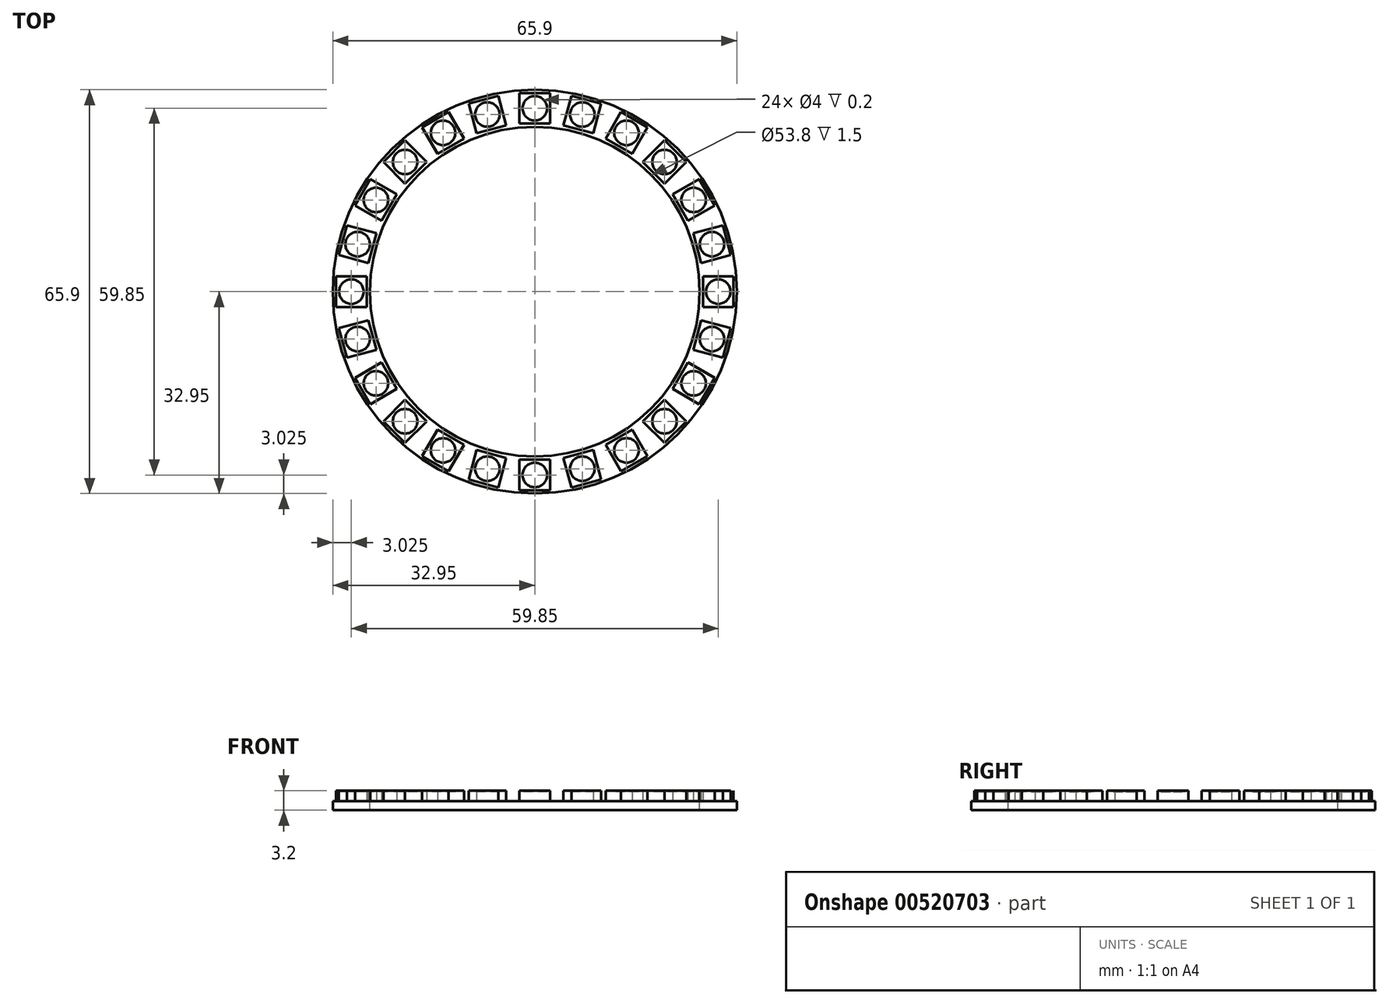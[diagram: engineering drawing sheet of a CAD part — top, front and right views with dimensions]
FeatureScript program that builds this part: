
annotation { "Feature Type Name" : "Feature", "Feature Type Description" : "" }
export const myFeature = defineFeature(function(context is Context, id is Id, definition is map)
    precondition{}
    {
        {
            assignVariable(context, id + "F0", {"name" : "LED_PCB_height", "anyValue" : 1.5 * mm});
        }
        {
            assignVariable(context, id + "F1", {"name" : "LED_case_height", "anyValue" : 1.7 * mm});
        }
        {
            assignVariable(context, id + "F2", {"name" : "LED_lens_height", "anyValue" : 1.5 * mm});
        }
        {
            var Q0;
            Q0=qCreatedBy(makeId("Top.planeOp"),FACE);
            var sketch = newSketch(context, id + "F3", { "sketchPlane" : qUnion([Q0])});
            skCircle(sketch, "E0", {"center": v(0, 0) * mm, "radius": 26.9 * mm});
            skCircle(sketch, "E1", {"center": v(0, 0) * mm, "radius": 32.95 * mm});
            skLineSegment(sketch, "E2.bottom", {"start": v(-2.5, 32.43) * mm, "end": v(2.5, 32.43) * mm});
            skLineSegment(sketch, "E2.top", {"start": v(-2.5, 27.43) * mm, "end": v(2.5, 27.43) * mm});
            skLineSegment(sketch, "E2.left", {"start": v(-2.5, 32.43) * mm, "end": v(-2.5, 27.43) * mm});
            skLineSegment(sketch, "E2.right", {"start": v(2.5, 32.43) * mm, "end": v(2.5, 27.43) * mm});
            skLineSegment(sketch, "E3", {"start": v(0, 32.43) * mm, "end": v(0, 32.95) * mm, "construction": true});
            skLineSegment(sketch, "E4", {"start": v(0, 27.43) * mm, "end": v(0, 26.9) * mm, "construction": true});
            skLineSegment(sketch, "E5", {"start": v(-2.5, 32.43) * mm, "end": v(2.5, 27.43) * mm, "construction": true});
            skLineSegment(sketch, "E6", {"start": v(2.5, 32.43) * mm, "end": v(-2.5, 27.43) * mm, "construction": true});
            skCircle(sketch, "E7", {"center": v(0, 29.93) * mm, "radius": 2 * mm});
            skCircle(sketch, "E8.1.0", {"center": v(-7.75, 28.9) * mm, "radius": 2 * mm});
            skLineSegment(sketch, "E8.1.1", {"start": v(-10.8, 30.67) * mm, "end": v(-5.98, 31.97) * mm});
            skLineSegment(sketch, "E8.1.2", {"start": v(-10.8, 30.67) * mm, "end": v(-9.51, 25.84) * mm});
            skLineSegment(sketch, "E8.1.3", {"start": v(-9.51, 25.84) * mm, "end": v(-4.68, 27.14) * mm});
            skLineSegment(sketch, "E8.1.4", {"start": v(-5.98, 31.97) * mm, "end": v(-4.68, 27.14) * mm});
            skCircle(sketch, "E8.2.0", {"center": v(-14.96, 25.92) * mm, "radius": 2 * mm});
            skLineSegment(sketch, "E8.2.1", {"start": v(-18.38, 26.83) * mm, "end": v(-14.05, 29.33) * mm});
            skLineSegment(sketch, "E8.2.2", {"start": v(-18.38, 26.83) * mm, "end": v(-15.88, 22.5) * mm});
            skLineSegment(sketch, "E8.2.3", {"start": v(-15.88, 22.5) * mm, "end": v(-11.55, 25) * mm});
            skLineSegment(sketch, "E8.2.4", {"start": v(-14.05, 29.33) * mm, "end": v(-11.55, 25) * mm});
            skCircle(sketch, "E8.3.0", {"center": v(-21.16, 21.16) * mm, "radius": 2 * mm});
            skLineSegment(sketch, "E8.3.1", {"start": v(-24.7, 21.16) * mm, "end": v(-21.16, 24.7) * mm});
            skLineSegment(sketch, "E8.3.2", {"start": v(-24.7, 21.16) * mm, "end": v(-21.16, 17.62) * mm});
            skLineSegment(sketch, "E8.3.3", {"start": v(-21.16, 17.62) * mm, "end": v(-17.62, 21.16) * mm});
            skLineSegment(sketch, "E8.3.4", {"start": v(-21.16, 24.7) * mm, "end": v(-17.62, 21.16) * mm});
            skCircle(sketch, "E8.4.0", {"center": v(-25.92, 14.96) * mm, "radius": 2 * mm});
            skLineSegment(sketch, "E8.4.1", {"start": v(-29.33, 14.05) * mm, "end": v(-26.83, 18.38) * mm});
            skLineSegment(sketch, "E8.4.2", {"start": v(-29.33, 14.05) * mm, "end": v(-25, 11.55) * mm});
            skLineSegment(sketch, "E8.4.3", {"start": v(-25, 11.55) * mm, "end": v(-22.5, 15.88) * mm});
            skLineSegment(sketch, "E8.4.4", {"start": v(-26.83, 18.38) * mm, "end": v(-22.5, 15.88) * mm});
            skCircle(sketch, "E8.5.0", {"center": v(-28.9, 7.75) * mm, "radius": 2 * mm});
            skLineSegment(sketch, "E8.5.1", {"start": v(-31.97, 5.98) * mm, "end": v(-30.67, 10.8) * mm});
            skLineSegment(sketch, "E8.5.2", {"start": v(-31.97, 5.98) * mm, "end": v(-27.14, 4.68) * mm});
            skLineSegment(sketch, "E8.5.3", {"start": v(-27.14, 4.68) * mm, "end": v(-25.84, 9.51) * mm});
            skLineSegment(sketch, "E8.5.4", {"start": v(-30.67, 10.8) * mm, "end": v(-25.84, 9.51) * mm});
            skCircle(sketch, "E8.6.0", {"center": v(-29.93, 0) * mm, "radius": 2 * mm});
            skLineSegment(sketch, "E8.6.1", {"start": v(-32.43, -2.5) * mm, "end": v(-32.43, 2.5) * mm});
            skLineSegment(sketch, "E8.6.2", {"start": v(-32.43, -2.5) * mm, "end": v(-27.43, -2.5) * mm});
            skLineSegment(sketch, "E8.6.3", {"start": v(-27.43, -2.5) * mm, "end": v(-27.43, 2.5) * mm});
            skLineSegment(sketch, "E8.6.4", {"start": v(-32.43, 2.5) * mm, "end": v(-27.43, 2.5) * mm});
            skCircle(sketch, "E8.7.0", {"center": v(-28.9, -7.75) * mm, "radius": 2 * mm});
            skLineSegment(sketch, "E8.7.1", {"start": v(-30.67, -10.8) * mm, "end": v(-31.97, -5.98) * mm});
            skLineSegment(sketch, "E8.7.2", {"start": v(-30.67, -10.8) * mm, "end": v(-25.84, -9.51) * mm});
            skLineSegment(sketch, "E8.7.3", {"start": v(-25.84, -9.51) * mm, "end": v(-27.14, -4.68) * mm});
            skLineSegment(sketch, "E8.7.4", {"start": v(-31.97, -5.98) * mm, "end": v(-27.14, -4.68) * mm});
            skCircle(sketch, "E8.8.0", {"center": v(-25.92, -14.96) * mm, "radius": 2 * mm});
            skLineSegment(sketch, "E8.8.1", {"start": v(-26.83, -18.38) * mm, "end": v(-29.33, -14.05) * mm});
            skLineSegment(sketch, "E8.8.2", {"start": v(-26.83, -18.38) * mm, "end": v(-22.5, -15.88) * mm});
            skLineSegment(sketch, "E8.8.3", {"start": v(-22.5, -15.88) * mm, "end": v(-25, -11.55) * mm});
            skLineSegment(sketch, "E8.8.4", {"start": v(-29.33, -14.05) * mm, "end": v(-25, -11.55) * mm});
            skCircle(sketch, "E8.9.0", {"center": v(-21.16, -21.16) * mm, "radius": 2 * mm});
            skLineSegment(sketch, "E8.9.1", {"start": v(-21.16, -24.7) * mm, "end": v(-24.7, -21.16) * mm});
            skLineSegment(sketch, "E8.9.2", {"start": v(-21.16, -24.7) * mm, "end": v(-17.62, -21.16) * mm});
            skLineSegment(sketch, "E8.9.3", {"start": v(-17.62, -21.16) * mm, "end": v(-21.16, -17.62) * mm});
            skLineSegment(sketch, "E8.9.4", {"start": v(-24.7, -21.16) * mm, "end": v(-21.16, -17.62) * mm});
            skCircle(sketch, "E8.10.0", {"center": v(-14.96, -25.92) * mm, "radius": 2 * mm});
            skLineSegment(sketch, "E8.10.1", {"start": v(-14.05, -29.33) * mm, "end": v(-18.38, -26.83) * mm});
            skLineSegment(sketch, "E8.10.2", {"start": v(-14.05, -29.33) * mm, "end": v(-11.55, -25) * mm});
            skLineSegment(sketch, "E8.10.3", {"start": v(-11.55, -25) * mm, "end": v(-15.88, -22.5) * mm});
            skLineSegment(sketch, "E8.10.4", {"start": v(-18.38, -26.83) * mm, "end": v(-15.88, -22.5) * mm});
            skCircle(sketch, "E8.11.0", {"center": v(-7.75, -28.9) * mm, "radius": 2 * mm});
            skLineSegment(sketch, "E8.11.1", {"start": v(-5.98, -31.97) * mm, "end": v(-10.8, -30.67) * mm});
            skLineSegment(sketch, "E8.11.2", {"start": v(-5.98, -31.97) * mm, "end": v(-4.68, -27.14) * mm});
            skLineSegment(sketch, "E8.11.3", {"start": v(-4.68, -27.14) * mm, "end": v(-9.51, -25.84) * mm});
            skLineSegment(sketch, "E8.11.4", {"start": v(-10.8, -30.67) * mm, "end": v(-9.51, -25.84) * mm});
            skCircle(sketch, "E8.12.0", {"center": v(0, -29.93) * mm, "radius": 2 * mm});
            skLineSegment(sketch, "E8.12.1", {"start": v(2.5, -32.43) * mm, "end": v(-2.5, -32.43) * mm});
            skLineSegment(sketch, "E8.12.2", {"start": v(2.5, -32.43) * mm, "end": v(2.5, -27.43) * mm});
            skLineSegment(sketch, "E8.12.3", {"start": v(2.5, -27.43) * mm, "end": v(-2.5, -27.43) * mm});
            skLineSegment(sketch, "E8.12.4", {"start": v(-2.5, -32.43) * mm, "end": v(-2.5, -27.43) * mm});
            skCircle(sketch, "E8.13.0", {"center": v(7.75, -28.9) * mm, "radius": 2 * mm});
            skLineSegment(sketch, "E8.13.1", {"start": v(10.8, -30.67) * mm, "end": v(5.98, -31.97) * mm});
            skLineSegment(sketch, "E8.13.2", {"start": v(10.8, -30.67) * mm, "end": v(9.51, -25.84) * mm});
            skLineSegment(sketch, "E8.13.3", {"start": v(9.51, -25.84) * mm, "end": v(4.68, -27.14) * mm});
            skLineSegment(sketch, "E8.13.4", {"start": v(5.98, -31.97) * mm, "end": v(4.68, -27.14) * mm});
            skCircle(sketch, "E8.14.0", {"center": v(14.96, -25.92) * mm, "radius": 2 * mm});
            skLineSegment(sketch, "E8.14.1", {"start": v(18.38, -26.83) * mm, "end": v(14.05, -29.33) * mm});
            skLineSegment(sketch, "E8.14.2", {"start": v(18.38, -26.83) * mm, "end": v(15.88, -22.5) * mm});
            skLineSegment(sketch, "E8.14.3", {"start": v(15.88, -22.5) * mm, "end": v(11.55, -25) * mm});
            skLineSegment(sketch, "E8.14.4", {"start": v(14.05, -29.33) * mm, "end": v(11.55, -25) * mm});
            skCircle(sketch, "E8.15.0", {"center": v(21.16, -21.16) * mm, "radius": 2 * mm});
            skLineSegment(sketch, "E8.15.1", {"start": v(24.7, -21.16) * mm, "end": v(21.16, -24.7) * mm});
            skLineSegment(sketch, "E8.15.2", {"start": v(24.7, -21.16) * mm, "end": v(21.16, -17.62) * mm});
            skLineSegment(sketch, "E8.15.3", {"start": v(21.16, -17.62) * mm, "end": v(17.62, -21.16) * mm});
            skLineSegment(sketch, "E8.15.4", {"start": v(21.16, -24.7) * mm, "end": v(17.62, -21.16) * mm});
            skCircle(sketch, "E8.16.0", {"center": v(25.92, -14.96) * mm, "radius": 2 * mm});
            skLineSegment(sketch, "E8.16.1", {"start": v(29.33, -14.05) * mm, "end": v(26.83, -18.38) * mm});
            skLineSegment(sketch, "E8.16.2", {"start": v(29.33, -14.05) * mm, "end": v(25, -11.55) * mm});
            skLineSegment(sketch, "E8.16.3", {"start": v(25, -11.55) * mm, "end": v(22.5, -15.88) * mm});
            skLineSegment(sketch, "E8.16.4", {"start": v(26.83, -18.38) * mm, "end": v(22.5, -15.88) * mm});
            skCircle(sketch, "E8.17.0", {"center": v(28.9, -7.75) * mm, "radius": 2 * mm});
            skLineSegment(sketch, "E8.17.1", {"start": v(31.97, -5.98) * mm, "end": v(30.67, -10.8) * mm});
            skLineSegment(sketch, "E8.17.2", {"start": v(31.97, -5.98) * mm, "end": v(27.14, -4.68) * mm});
            skLineSegment(sketch, "E8.17.3", {"start": v(27.14, -4.68) * mm, "end": v(25.84, -9.51) * mm});
            skLineSegment(sketch, "E8.17.4", {"start": v(30.67, -10.8) * mm, "end": v(25.84, -9.51) * mm});
            skCircle(sketch, "E8.18.0", {"center": v(29.93, 0) * mm, "radius": 2 * mm});
            skLineSegment(sketch, "E8.18.1", {"start": v(32.43, 2.5) * mm, "end": v(32.43, -2.5) * mm});
            skLineSegment(sketch, "E8.18.2", {"start": v(32.43, 2.5) * mm, "end": v(27.43, 2.5) * mm});
            skLineSegment(sketch, "E8.18.3", {"start": v(27.43, 2.5) * mm, "end": v(27.43, -2.5) * mm});
            skLineSegment(sketch, "E8.18.4", {"start": v(32.43, -2.5) * mm, "end": v(27.43, -2.5) * mm});
            skCircle(sketch, "E8.19.0", {"center": v(28.9, 7.75) * mm, "radius": 2 * mm});
            skLineSegment(sketch, "E8.19.1", {"start": v(30.67, 10.8) * mm, "end": v(31.97, 5.98) * mm});
            skLineSegment(sketch, "E8.19.2", {"start": v(30.67, 10.8) * mm, "end": v(25.84, 9.51) * mm});
            skLineSegment(sketch, "E8.19.3", {"start": v(25.84, 9.51) * mm, "end": v(27.14, 4.68) * mm});
            skLineSegment(sketch, "E8.19.4", {"start": v(31.97, 5.98) * mm, "end": v(27.14, 4.68) * mm});
            skCircle(sketch, "E8.20.0", {"center": v(25.92, 14.96) * mm, "radius": 2 * mm});
            skLineSegment(sketch, "E8.20.1", {"start": v(26.83, 18.38) * mm, "end": v(29.33, 14.05) * mm});
            skLineSegment(sketch, "E8.20.2", {"start": v(26.83, 18.38) * mm, "end": v(22.5, 15.88) * mm});
            skLineSegment(sketch, "E8.20.3", {"start": v(22.5, 15.88) * mm, "end": v(25, 11.55) * mm});
            skLineSegment(sketch, "E8.20.4", {"start": v(29.33, 14.05) * mm, "end": v(25, 11.55) * mm});
            skCircle(sketch, "E8.21.0", {"center": v(21.16, 21.16) * mm, "radius": 2 * mm});
            skLineSegment(sketch, "E8.21.1", {"start": v(21.16, 24.7) * mm, "end": v(24.7, 21.16) * mm});
            skLineSegment(sketch, "E8.21.2", {"start": v(21.16, 24.7) * mm, "end": v(17.62, 21.16) * mm});
            skLineSegment(sketch, "E8.21.3", {"start": v(17.62, 21.16) * mm, "end": v(21.16, 17.62) * mm});
            skLineSegment(sketch, "E8.21.4", {"start": v(24.7, 21.16) * mm, "end": v(21.16, 17.62) * mm});
            skCircle(sketch, "E8.22.0", {"center": v(14.96, 25.92) * mm, "radius": 2 * mm});
            skLineSegment(sketch, "E8.22.1", {"start": v(14.05, 29.33) * mm, "end": v(18.38, 26.83) * mm});
            skLineSegment(sketch, "E8.22.2", {"start": v(14.05, 29.33) * mm, "end": v(11.55, 25) * mm});
            skLineSegment(sketch, "E8.22.3", {"start": v(11.55, 25) * mm, "end": v(15.88, 22.5) * mm});
            skLineSegment(sketch, "E8.22.4", {"start": v(18.38, 26.83) * mm, "end": v(15.88, 22.5) * mm});
            skCircle(sketch, "E8.23.0", {"center": v(7.75, 28.9) * mm, "radius": 2 * mm});
            skLineSegment(sketch, "E8.23.1", {"start": v(5.98, 31.97) * mm, "end": v(10.8, 30.67) * mm});
            skLineSegment(sketch, "E8.23.2", {"start": v(5.98, 31.97) * mm, "end": v(4.68, 27.14) * mm});
            skLineSegment(sketch, "E8.23.3", {"start": v(4.68, 27.14) * mm, "end": v(9.51, 25.84) * mm});
            skLineSegment(sketch, "E8.23.4", {"start": v(10.8, 30.67) * mm, "end": v(9.51, 25.84) * mm});
            skSolve(sketch);
        }
        {
            var Q0;
            Q0=makeQuery(id+"F3.imprint","IMPRINT",FACE,{"disambiguationData":[TD([[makeQuery(id+"F3.imprint","IMPRINT",EDGE,{"derivedFrom":sQuery(id+"F3.wireOp",EDGE,"E0")}),-1.0]])]});
            var Q1;
            Q1=makeQuery(id+"F3.imprint","IMPRINT",FACE,{"disambiguationData":[TD([[makeQuery(id+"F3.imprint","IMPRINT",EDGE,{"derivedFrom":sQuery(id+"F3.wireOp",EDGE,"E8.3.0")}),1.0]])]});
            var Q2;
            Q2=makeQuery(id+"F3.imprint","IMPRINT",FACE,{"disambiguationData":[TD([[makeQuery(id+"F3.imprint","IMPRINT",EDGE,{"derivedFrom":sQuery(id+"F3.wireOp",EDGE,"E8.3.0")}),-1.0]])]});
            var Q3;
            Q3=makeQuery(id+"F3.imprint","IMPRINT",FACE,{"disambiguationData":[TD([[makeQuery(id+"F3.imprint","IMPRINT",EDGE,{"derivedFrom":sQuery(id+"F3.wireOp",EDGE,"E8.2.0")}),-1.0]])]});
            var Q4;
            Q4=makeQuery(id+"F3.imprint","IMPRINT",FACE,{"disambiguationData":[TD([[makeQuery(id+"F3.imprint","IMPRINT",EDGE,{"derivedFrom":sQuery(id+"F3.wireOp",EDGE,"E8.2.0")}),1.0]])]});
            var Q5;
            Q5=makeQuery(id+"F3.imprint","IMPRINT",FACE,{"disambiguationData":[TD([[makeQuery(id+"F3.imprint","IMPRINT",EDGE,{"derivedFrom":sQuery(id+"F3.wireOp",EDGE,"E8.1.0")}),-1.0]])]});
            var Q6;
            Q6=makeQuery(id+"F3.imprint","IMPRINT",FACE,{"disambiguationData":[TD([[makeQuery(id+"F3.imprint","IMPRINT",EDGE,{"derivedFrom":sQuery(id+"F3.wireOp",EDGE,"E8.1.0")}),1.0]])]});
            var Q7;
            Q7=makeQuery(id+"F3.imprint","IMPRINT",FACE,{"disambiguationData":[TD([[makeQuery(id+"F3.imprint","IMPRINT",EDGE,{"derivedFrom":sQuery(id+"F3.wireOp",EDGE,"E7")}),1.0]])]});
            var Q8;
            Q8=makeQuery(id+"F3.imprint","IMPRINT",FACE,{"disambiguationData":[TD([[makeQuery(id+"F3.imprint","IMPRINT",EDGE,{"derivedFrom":sQuery(id+"F3.wireOp",EDGE,"E2.bottom")}),-1.0]])]});
            var Q9;
            Q9=makeQuery(id+"F3.imprint","IMPRINT",FACE,{"disambiguationData":[TD([[makeQuery(id+"F3.imprint","IMPRINT",EDGE,{"derivedFrom":sQuery(id+"F3.wireOp",EDGE,"E8.23.0")}),1.0]])]});
            var Q10;
            Q10=makeQuery(id+"F3.imprint","IMPRINT",FACE,{"disambiguationData":[TD([[makeQuery(id+"F3.imprint","IMPRINT",EDGE,{"derivedFrom":sQuery(id+"F3.wireOp",EDGE,"E8.23.0")}),-1.0]])]});
            var Q11;
            Q11=makeQuery(id+"F3.imprint","IMPRINT",FACE,{"disambiguationData":[TD([[makeQuery(id+"F3.imprint","IMPRINT",EDGE,{"derivedFrom":sQuery(id+"F3.wireOp",EDGE,"E8.22.0")}),1.0]])]});
            var Q12;
            Q12=makeQuery(id+"F3.imprint","IMPRINT",FACE,{"disambiguationData":[TD([[makeQuery(id+"F3.imprint","IMPRINT",EDGE,{"derivedFrom":sQuery(id+"F3.wireOp",EDGE,"E8.22.0")}),-1.0]])]});
            var Q13;
            Q13=makeQuery(id+"F3.imprint","IMPRINT",FACE,{"disambiguationData":[TD([[makeQuery(id+"F3.imprint","IMPRINT",EDGE,{"derivedFrom":sQuery(id+"F3.wireOp",EDGE,"E8.21.0")}),1.0]])]});
            var Q14;
            Q14=makeQuery(id+"F3.imprint","IMPRINT",FACE,{"disambiguationData":[TD([[makeQuery(id+"F3.imprint","IMPRINT",EDGE,{"derivedFrom":sQuery(id+"F3.wireOp",EDGE,"E8.21.0")}),-1.0]])]});
            var Q15;
            Q15=makeQuery(id+"F3.imprint","IMPRINT",FACE,{"disambiguationData":[TD([[makeQuery(id+"F3.imprint","IMPRINT",EDGE,{"derivedFrom":sQuery(id+"F3.wireOp",EDGE,"E8.20.0")}),1.0]])]});
            var Q16;
            Q16=makeQuery(id+"F3.imprint","IMPRINT",FACE,{"disambiguationData":[TD([[makeQuery(id+"F3.imprint","IMPRINT",EDGE,{"derivedFrom":sQuery(id+"F3.wireOp",EDGE,"E8.20.0")}),-1.0]])]});
            var Q17;
            Q17=makeQuery(id+"F3.imprint","IMPRINT",FACE,{"disambiguationData":[TD([[makeQuery(id+"F3.imprint","IMPRINT",EDGE,{"derivedFrom":sQuery(id+"F3.wireOp",EDGE,"E8.19.0")}),1.0]])]});
            var Q18;
            Q18=makeQuery(id+"F3.imprint","IMPRINT",FACE,{"disambiguationData":[TD([[makeQuery(id+"F3.imprint","IMPRINT",EDGE,{"derivedFrom":sQuery(id+"F3.wireOp",EDGE,"E8.19.0")}),-1.0]])]});
            var Q19;
            Q19=makeQuery(id+"F3.imprint","IMPRINT",FACE,{"disambiguationData":[TD([[makeQuery(id+"F3.imprint","IMPRINT",EDGE,{"derivedFrom":sQuery(id+"F3.wireOp",EDGE,"E8.18.0")}),1.0]])]});
            var Q20;
            Q20=makeQuery(id+"F3.imprint","IMPRINT",FACE,{"disambiguationData":[TD([[makeQuery(id+"F3.imprint","IMPRINT",EDGE,{"derivedFrom":sQuery(id+"F3.wireOp",EDGE,"E8.18.0")}),-1.0]])]});
            var Q21;
            Q21=makeQuery(id+"F3.imprint","IMPRINT",FACE,{"disambiguationData":[TD([[makeQuery(id+"F3.imprint","IMPRINT",EDGE,{"derivedFrom":sQuery(id+"F3.wireOp",EDGE,"E8.17.0")}),1.0]])]});
            var Q22;
            Q22=makeQuery(id+"F3.imprint","IMPRINT",FACE,{"disambiguationData":[TD([[makeQuery(id+"F3.imprint","IMPRINT",EDGE,{"derivedFrom":sQuery(id+"F3.wireOp",EDGE,"E8.17.0")}),-1.0]])]});
            var Q23;
            Q23=makeQuery(id+"F3.imprint","IMPRINT",FACE,{"disambiguationData":[TD([[makeQuery(id+"F3.imprint","IMPRINT",EDGE,{"derivedFrom":sQuery(id+"F3.wireOp",EDGE,"E8.5.0")}),1.0]])]});
            var Q24;
            Q24=makeQuery(id+"F3.imprint","IMPRINT",FACE,{"disambiguationData":[TD([[makeQuery(id+"F3.imprint","IMPRINT",EDGE,{"derivedFrom":sQuery(id+"F3.wireOp",EDGE,"E8.5.0")}),-1.0]])]});
            var Q25;
            Q25=makeQuery(id+"F3.imprint","IMPRINT",FACE,{"disambiguationData":[TD([[makeQuery(id+"F3.imprint","IMPRINT",EDGE,{"derivedFrom":sQuery(id+"F3.wireOp",EDGE,"E8.4.0")}),1.0]])]});
            var Q26;
            Q26=makeQuery(id+"F3.imprint","IMPRINT",FACE,{"disambiguationData":[TD([[makeQuery(id+"F3.imprint","IMPRINT",EDGE,{"derivedFrom":sQuery(id+"F3.wireOp",EDGE,"E8.4.0")}),-1.0]])]});
            var Q27;
            Q27=makeQuery(id+"F3.imprint","IMPRINT",FACE,{"disambiguationData":[TD([[makeQuery(id+"F3.imprint","IMPRINT",EDGE,{"derivedFrom":sQuery(id+"F3.wireOp",EDGE,"E8.6.0")}),-1.0]])]});
            var Q28;
            Q28=makeQuery(id+"F3.imprint","IMPRINT",FACE,{"disambiguationData":[TD([[makeQuery(id+"F3.imprint","IMPRINT",EDGE,{"derivedFrom":sQuery(id+"F3.wireOp",EDGE,"E8.6.0")}),1.0]])]});
            var Q29;
            Q29=makeQuery(id+"F3.imprint","IMPRINT",FACE,{"disambiguationData":[TD([[makeQuery(id+"F3.imprint","IMPRINT",EDGE,{"derivedFrom":sQuery(id+"F3.wireOp",EDGE,"E8.7.0")}),1.0]])]});
            var Q30;
            Q30=makeQuery(id+"F3.imprint","IMPRINT",FACE,{"disambiguationData":[TD([[makeQuery(id+"F3.imprint","IMPRINT",EDGE,{"derivedFrom":sQuery(id+"F3.wireOp",EDGE,"E8.7.0")}),-1.0]])]});
            var Q31;
            Q31=makeQuery(id+"F3.imprint","IMPRINT",FACE,{"disambiguationData":[TD([[makeQuery(id+"F3.imprint","IMPRINT",EDGE,{"derivedFrom":sQuery(id+"F3.wireOp",EDGE,"E8.8.0")}),1.0]])]});
            var Q32;
            Q32=makeQuery(id+"F3.imprint","IMPRINT",FACE,{"disambiguationData":[TD([[makeQuery(id+"F3.imprint","IMPRINT",EDGE,{"derivedFrom":sQuery(id+"F3.wireOp",EDGE,"E8.9.0")}),1.0]])]});
            var Q33;
            Q33=makeQuery(id+"F3.imprint","IMPRINT",FACE,{"disambiguationData":[TD([[makeQuery(id+"F3.imprint","IMPRINT",EDGE,{"derivedFrom":sQuery(id+"F3.wireOp",EDGE,"E8.8.0")}),-1.0]])]});
            var Q34;
            Q34=makeQuery(id+"F3.imprint","IMPRINT",FACE,{"disambiguationData":[TD([[makeQuery(id+"F3.imprint","IMPRINT",EDGE,{"derivedFrom":sQuery(id+"F3.wireOp",EDGE,"E8.9.0")}),-1.0]])]});
            var Q35;
            Q35=makeQuery(id+"F3.imprint","IMPRINT",FACE,{"disambiguationData":[TD([[makeQuery(id+"F3.imprint","IMPRINT",EDGE,{"derivedFrom":sQuery(id+"F3.wireOp",EDGE,"E8.10.0")}),-1.0]])]});
            var Q36;
            Q36=makeQuery(id+"F3.imprint","IMPRINT",FACE,{"disambiguationData":[TD([[makeQuery(id+"F3.imprint","IMPRINT",EDGE,{"derivedFrom":sQuery(id+"F3.wireOp",EDGE,"E8.10.0")}),1.0]])]});
            var Q37;
            Q37=makeQuery(id+"F3.imprint","IMPRINT",FACE,{"disambiguationData":[TD([[makeQuery(id+"F3.imprint","IMPRINT",EDGE,{"derivedFrom":sQuery(id+"F3.wireOp",EDGE,"E8.11.0")}),-1.0]])]});
            var Q38;
            Q38=makeQuery(id+"F3.imprint","IMPRINT",FACE,{"disambiguationData":[TD([[makeQuery(id+"F3.imprint","IMPRINT",EDGE,{"derivedFrom":sQuery(id+"F3.wireOp",EDGE,"E8.11.0")}),1.0]])]});
            var Q39;
            Q39=makeQuery(id+"F3.imprint","IMPRINT",FACE,{"disambiguationData":[TD([[makeQuery(id+"F3.imprint","IMPRINT",EDGE,{"derivedFrom":sQuery(id+"F3.wireOp",EDGE,"E8.12.0")}),1.0]])]});
            var Q40;
            Q40=makeQuery(id+"F3.imprint","IMPRINT",FACE,{"disambiguationData":[TD([[makeQuery(id+"F3.imprint","IMPRINT",EDGE,{"derivedFrom":sQuery(id+"F3.wireOp",EDGE,"E8.12.0")}),-1.0]])]});
            var Q41;
            Q41=makeQuery(id+"F3.imprint","IMPRINT",FACE,{"disambiguationData":[TD([[makeQuery(id+"F3.imprint","IMPRINT",EDGE,{"derivedFrom":sQuery(id+"F3.wireOp",EDGE,"E8.13.0")}),-1.0]])]});
            var Q42;
            Q42=makeQuery(id+"F3.imprint","IMPRINT",FACE,{"disambiguationData":[TD([[makeQuery(id+"F3.imprint","IMPRINT",EDGE,{"derivedFrom":sQuery(id+"F3.wireOp",EDGE,"E8.13.0")}),1.0]])]});
            var Q43;
            Q43=makeQuery(id+"F3.imprint","IMPRINT",FACE,{"disambiguationData":[TD([[makeQuery(id+"F3.imprint","IMPRINT",EDGE,{"derivedFrom":sQuery(id+"F3.wireOp",EDGE,"E8.14.0")}),-1.0]])]});
            var Q44;
            Q44=makeQuery(id+"F3.imprint","IMPRINT",FACE,{"disambiguationData":[TD([[makeQuery(id+"F3.imprint","IMPRINT",EDGE,{"derivedFrom":sQuery(id+"F3.wireOp",EDGE,"E8.14.0")}),1.0]])]});
            var Q45;
            Q45=makeQuery(id+"F3.imprint","IMPRINT",FACE,{"disambiguationData":[TD([[makeQuery(id+"F3.imprint","IMPRINT",EDGE,{"derivedFrom":sQuery(id+"F3.wireOp",EDGE,"E8.15.0")}),-1.0]])]});
            var Q46;
            Q46=makeQuery(id+"F3.imprint","IMPRINT",FACE,{"disambiguationData":[TD([[makeQuery(id+"F3.imprint","IMPRINT",EDGE,{"derivedFrom":sQuery(id+"F3.wireOp",EDGE,"E8.15.0")}),1.0]])]});
            var Q47;
            Q47=makeQuery(id+"F3.imprint","IMPRINT",FACE,{"disambiguationData":[TD([[makeQuery(id+"F3.imprint","IMPRINT",EDGE,{"derivedFrom":sQuery(id+"F3.wireOp",EDGE,"E8.16.0")}),-1.0]])]});
            var Q48;
            Q48=makeQuery(id+"F3.imprint","IMPRINT",FACE,{"disambiguationData":[TD([[makeQuery(id+"F3.imprint","IMPRINT",EDGE,{"derivedFrom":sQuery(id+"F3.wireOp",EDGE,"E8.16.0")}),1.0]])]});
            extrude(context, id + "F4", {"entities" : qUnion([Q0, Q1, Q2, Q3, Q4, Q5, Q6, Q7, Q8, Q9, Q10, Q11, Q12, Q13, Q14, Q15, Q16, Q17, Q18, Q19, Q20, Q21, Q22, Q23, Q24, Q25, Q26, Q27, Q28, Q29, Q30, Q31, Q32, Q33, Q34, Q35, Q36, Q37, Q38, Q39, Q40, Q41, Q42, Q43, Q44, Q45, Q46, Q47, Q48]), "oppositeDirection" : true, "depth" : getVariable(context, 'LED_PCB_height'), "offsetDistance" : 25 * mm});
        }
        {
            var Q0;
            Q0=makeQuery(id+"F3.imprint","IMPRINT",FACE,{"disambiguationData":[TD([[makeQuery(id+"F3.imprint","IMPRINT",EDGE,{"derivedFrom":sQuery(id+"F3.wireOp",EDGE,"E8.23.0")}),-1.0]])]});
            var Q1;
            Q1=makeQuery(id+"F3.imprint","IMPRINT",FACE,{"disambiguationData":[TD([[makeQuery(id+"F3.imprint","IMPRINT",EDGE,{"derivedFrom":sQuery(id+"F3.wireOp",EDGE,"E8.22.0")}),-1.0]])]});
            var Q2;
            Q2=makeQuery(id+"F3.imprint","IMPRINT",FACE,{"disambiguationData":[TD([[makeQuery(id+"F3.imprint","IMPRINT",EDGE,{"derivedFrom":sQuery(id+"F3.wireOp",EDGE,"E8.21.0")}),-1.0]])]});
            var Q3;
            Q3=makeQuery(id+"F3.imprint","IMPRINT",FACE,{"disambiguationData":[TD([[makeQuery(id+"F3.imprint","IMPRINT",EDGE,{"derivedFrom":sQuery(id+"F3.wireOp",EDGE,"E8.20.0")}),-1.0]])]});
            var Q4;
            Q4=makeQuery(id+"F3.imprint","IMPRINT",FACE,{"disambiguationData":[TD([[makeQuery(id+"F3.imprint","IMPRINT",EDGE,{"derivedFrom":sQuery(id+"F3.wireOp",EDGE,"E8.19.0")}),-1.0]])]});
            var Q5;
            Q5=makeQuery(id+"F3.imprint","IMPRINT",FACE,{"disambiguationData":[TD([[makeQuery(id+"F3.imprint","IMPRINT",EDGE,{"derivedFrom":sQuery(id+"F3.wireOp",EDGE,"E8.18.0")}),-1.0]])]});
            var Q6;
            Q6=makeQuery(id+"F3.imprint","IMPRINT",FACE,{"disambiguationData":[TD([[makeQuery(id+"F3.imprint","IMPRINT",EDGE,{"derivedFrom":sQuery(id+"F3.wireOp",EDGE,"E8.17.0")}),-1.0]])]});
            var Q7;
            Q7=makeQuery(id+"F3.imprint","IMPRINT",FACE,{"disambiguationData":[TD([[makeQuery(id+"F3.imprint","IMPRINT",EDGE,{"derivedFrom":sQuery(id+"F3.wireOp",EDGE,"E8.1.0")}),-1.0]])]});
            var Q8;
            Q8=makeQuery(id+"F3.imprint","IMPRINT",FACE,{"disambiguationData":[TD([[makeQuery(id+"F3.imprint","IMPRINT",EDGE,{"derivedFrom":sQuery(id+"F3.wireOp",EDGE,"E2.bottom")}),-1.0]])]});
            var Q9;
            Q9=makeQuery(id+"F3.imprint","IMPRINT",FACE,{"disambiguationData":[TD([[makeQuery(id+"F3.imprint","IMPRINT",EDGE,{"derivedFrom":sQuery(id+"F3.wireOp",EDGE,"E8.2.0")}),-1.0]])]});
            var Q10;
            Q10=makeQuery(id+"F3.imprint","IMPRINT",FACE,{"disambiguationData":[TD([[makeQuery(id+"F3.imprint","IMPRINT",EDGE,{"derivedFrom":sQuery(id+"F3.wireOp",EDGE,"E8.3.0")}),-1.0]])]});
            var Q11;
            Q11=makeQuery(id+"F3.imprint","IMPRINT",FACE,{"disambiguationData":[TD([[makeQuery(id+"F3.imprint","IMPRINT",EDGE,{"derivedFrom":sQuery(id+"F3.wireOp",EDGE,"E8.4.0")}),-1.0]])]});
            var Q12;
            Q12=makeQuery(id+"F3.imprint","IMPRINT",FACE,{"disambiguationData":[TD([[makeQuery(id+"F3.imprint","IMPRINT",EDGE,{"derivedFrom":sQuery(id+"F3.wireOp",EDGE,"E8.5.0")}),-1.0]])]});
            var Q13;
            Q13=makeQuery(id+"F3.imprint","IMPRINT",FACE,{"disambiguationData":[TD([[makeQuery(id+"F3.imprint","IMPRINT",EDGE,{"derivedFrom":sQuery(id+"F3.wireOp",EDGE,"E8.6.0")}),-1.0]])]});
            var Q14;
            Q14=makeQuery(id+"F3.imprint","IMPRINT",FACE,{"disambiguationData":[TD([[makeQuery(id+"F3.imprint","IMPRINT",EDGE,{"derivedFrom":sQuery(id+"F3.wireOp",EDGE,"E8.7.0")}),-1.0]])]});
            var Q15;
            Q15=makeQuery(id+"F3.imprint","IMPRINT",FACE,{"disambiguationData":[TD([[makeQuery(id+"F3.imprint","IMPRINT",EDGE,{"derivedFrom":sQuery(id+"F3.wireOp",EDGE,"E8.8.0")}),-1.0]])]});
            var Q16;
            Q16=makeQuery(id+"F3.imprint","IMPRINT",FACE,{"disambiguationData":[TD([[makeQuery(id+"F3.imprint","IMPRINT",EDGE,{"derivedFrom":sQuery(id+"F3.wireOp",EDGE,"E8.9.0")}),-1.0]])]});
            var Q17;
            Q17=makeQuery(id+"F3.imprint","IMPRINT",FACE,{"disambiguationData":[TD([[makeQuery(id+"F3.imprint","IMPRINT",EDGE,{"derivedFrom":sQuery(id+"F3.wireOp",EDGE,"E8.10.0")}),-1.0]])]});
            var Q18;
            Q18=makeQuery(id+"F3.imprint","IMPRINT",FACE,{"disambiguationData":[TD([[makeQuery(id+"F3.imprint","IMPRINT",EDGE,{"derivedFrom":sQuery(id+"F3.wireOp",EDGE,"E8.11.0")}),-1.0]])]});
            var Q19;
            Q19=makeQuery(id+"F3.imprint","IMPRINT",FACE,{"disambiguationData":[TD([[makeQuery(id+"F3.imprint","IMPRINT",EDGE,{"derivedFrom":sQuery(id+"F3.wireOp",EDGE,"E8.12.0")}),-1.0]])]});
            var Q20;
            Q20=makeQuery(id+"F3.imprint","IMPRINT",FACE,{"disambiguationData":[TD([[makeQuery(id+"F3.imprint","IMPRINT",EDGE,{"derivedFrom":sQuery(id+"F3.wireOp",EDGE,"E8.13.0")}),-1.0]])]});
            var Q21;
            Q21=makeQuery(id+"F3.imprint","IMPRINT",FACE,{"disambiguationData":[TD([[makeQuery(id+"F3.imprint","IMPRINT",EDGE,{"derivedFrom":sQuery(id+"F3.wireOp",EDGE,"E8.14.0")}),-1.0]])]});
            var Q22;
            Q22=makeQuery(id+"F3.imprint","IMPRINT",FACE,{"disambiguationData":[TD([[makeQuery(id+"F3.imprint","IMPRINT",EDGE,{"derivedFrom":sQuery(id+"F3.wireOp",EDGE,"E8.15.0")}),-1.0]])]});
            var Q23;
            Q23=makeQuery(id+"F3.imprint","IMPRINT",FACE,{"disambiguationData":[TD([[makeQuery(id+"F3.imprint","IMPRINT",EDGE,{"derivedFrom":sQuery(id+"F3.wireOp",EDGE,"E8.16.0")}),-1.0]])]});
            extrude(context, id + "F5", {"entities" : qUnion([Q0, Q1, Q2, Q3, Q4, Q5, Q6, Q7, Q8, Q9, Q10, Q11, Q12, Q13, Q14, Q15, Q16, Q17, Q18, Q19, Q20, Q21, Q22, Q23]), "operationType" : NewBodyOperationType.ADD, "depth" : getVariable(context, 'LED_case_height'), "offsetDistance" : 25 * mm});
        }
        {
            var Q0;
            Q0=makeQuery(id+"F3.imprint","IMPRINT",FACE,{"disambiguationData":[TD([[makeQuery(id+"F3.imprint","IMPRINT",EDGE,{"derivedFrom":sQuery(id+"F3.wireOp",EDGE,"E8.22.0")}),1.0]])]});
            var Q1;
            Q1=makeQuery(id+"F3.imprint","IMPRINT",FACE,{"disambiguationData":[TD([[makeQuery(id+"F3.imprint","IMPRINT",EDGE,{"derivedFrom":sQuery(id+"F3.wireOp",EDGE,"E8.23.0")}),1.0]])]});
            var Q2;
            Q2=makeQuery(id+"F3.imprint","IMPRINT",FACE,{"disambiguationData":[TD([[makeQuery(id+"F3.imprint","IMPRINT",EDGE,{"derivedFrom":sQuery(id+"F3.wireOp",EDGE,"E7")}),1.0]])]});
            var Q3;
            Q3=makeQuery(id+"F3.imprint","IMPRINT",FACE,{"disambiguationData":[TD([[makeQuery(id+"F3.imprint","IMPRINT",EDGE,{"derivedFrom":sQuery(id+"F3.wireOp",EDGE,"E8.1.0")}),1.0]])]});
            var Q4;
            Q4=makeQuery(id+"F3.imprint","IMPRINT",FACE,{"disambiguationData":[TD([[makeQuery(id+"F3.imprint","IMPRINT",EDGE,{"derivedFrom":sQuery(id+"F3.wireOp",EDGE,"E8.2.0")}),1.0]])]});
            var Q5;
            Q5=makeQuery(id+"F3.imprint","IMPRINT",FACE,{"disambiguationData":[TD([[makeQuery(id+"F3.imprint","IMPRINT",EDGE,{"derivedFrom":sQuery(id+"F3.wireOp",EDGE,"E8.21.0")}),1.0]])]});
            var Q6;
            Q6=makeQuery(id+"F3.imprint","IMPRINT",FACE,{"disambiguationData":[TD([[makeQuery(id+"F3.imprint","IMPRINT",EDGE,{"derivedFrom":sQuery(id+"F3.wireOp",EDGE,"E8.20.0")}),1.0]])]});
            var Q7;
            Q7=makeQuery(id+"F3.imprint","IMPRINT",FACE,{"disambiguationData":[TD([[makeQuery(id+"F3.imprint","IMPRINT",EDGE,{"derivedFrom":sQuery(id+"F3.wireOp",EDGE,"E8.19.0")}),1.0]])]});
            var Q8;
            Q8=makeQuery(id+"F3.imprint","IMPRINT",FACE,{"disambiguationData":[TD([[makeQuery(id+"F3.imprint","IMPRINT",EDGE,{"derivedFrom":sQuery(id+"F3.wireOp",EDGE,"E8.18.0")}),1.0]])]});
            var Q9;
            Q9=makeQuery(id+"F3.imprint","IMPRINT",FACE,{"disambiguationData":[TD([[makeQuery(id+"F3.imprint","IMPRINT",EDGE,{"derivedFrom":sQuery(id+"F3.wireOp",EDGE,"E8.17.0")}),1.0]])]});
            var Q10;
            Q10=makeQuery(id+"F3.imprint","IMPRINT",FACE,{"disambiguationData":[TD([[makeQuery(id+"F3.imprint","IMPRINT",EDGE,{"derivedFrom":sQuery(id+"F3.wireOp",EDGE,"E8.16.0")}),1.0]])]});
            var Q11;
            Q11=makeQuery(id+"F3.imprint","IMPRINT",FACE,{"disambiguationData":[TD([[makeQuery(id+"F3.imprint","IMPRINT",EDGE,{"derivedFrom":sQuery(id+"F3.wireOp",EDGE,"E8.15.0")}),1.0]])]});
            var Q12;
            Q12=makeQuery(id+"F3.imprint","IMPRINT",FACE,{"disambiguationData":[TD([[makeQuery(id+"F3.imprint","IMPRINT",EDGE,{"derivedFrom":sQuery(id+"F3.wireOp",EDGE,"E8.7.0")}),1.0]])]});
            var Q13;
            Q13=makeQuery(id+"F3.imprint","IMPRINT",FACE,{"disambiguationData":[TD([[makeQuery(id+"F3.imprint","IMPRINT",EDGE,{"derivedFrom":sQuery(id+"F3.wireOp",EDGE,"E8.14.0")}),1.0]])]});
            var Q14;
            Q14=makeQuery(id+"F3.imprint","IMPRINT",FACE,{"disambiguationData":[TD([[makeQuery(id+"F3.imprint","IMPRINT",EDGE,{"derivedFrom":sQuery(id+"F3.wireOp",EDGE,"E8.3.0")}),1.0]])]});
            var Q15;
            Q15=makeQuery(id+"F3.imprint","IMPRINT",FACE,{"disambiguationData":[TD([[makeQuery(id+"F3.imprint","IMPRINT",EDGE,{"derivedFrom":sQuery(id+"F3.wireOp",EDGE,"E8.4.0")}),1.0]])]});
            var Q16;
            Q16=makeQuery(id+"F3.imprint","IMPRINT",FACE,{"disambiguationData":[TD([[makeQuery(id+"F3.imprint","IMPRINT",EDGE,{"derivedFrom":sQuery(id+"F3.wireOp",EDGE,"E8.5.0")}),1.0]])]});
            var Q17;
            Q17=makeQuery(id+"F3.imprint","IMPRINT",FACE,{"disambiguationData":[TD([[makeQuery(id+"F3.imprint","IMPRINT",EDGE,{"derivedFrom":sQuery(id+"F3.wireOp",EDGE,"E8.6.0")}),1.0]])]});
            var Q18;
            Q18=makeQuery(id+"F3.imprint","IMPRINT",FACE,{"disambiguationData":[TD([[makeQuery(id+"F3.imprint","IMPRINT",EDGE,{"derivedFrom":sQuery(id+"F3.wireOp",EDGE,"E8.8.0")}),1.0]])]});
            var Q19;
            Q19=makeQuery(id+"F3.imprint","IMPRINT",FACE,{"disambiguationData":[TD([[makeQuery(id+"F3.imprint","IMPRINT",EDGE,{"derivedFrom":sQuery(id+"F3.wireOp",EDGE,"E8.9.0")}),1.0]])]});
            var Q20;
            Q20=makeQuery(id+"F3.imprint","IMPRINT",FACE,{"disambiguationData":[TD([[makeQuery(id+"F3.imprint","IMPRINT",EDGE,{"derivedFrom":sQuery(id+"F3.wireOp",EDGE,"E8.10.0")}),1.0]])]});
            var Q21;
            Q21=makeQuery(id+"F3.imprint","IMPRINT",FACE,{"disambiguationData":[TD([[makeQuery(id+"F3.imprint","IMPRINT",EDGE,{"derivedFrom":sQuery(id+"F3.wireOp",EDGE,"E8.11.0")}),1.0]])]});
            var Q22;
            Q22=makeQuery(id+"F3.imprint","IMPRINT",FACE,{"disambiguationData":[TD([[makeQuery(id+"F3.imprint","IMPRINT",EDGE,{"derivedFrom":sQuery(id+"F3.wireOp",EDGE,"E8.12.0")}),1.0]])]});
            var Q23;
            Q23=makeQuery(id+"F3.imprint","IMPRINT",FACE,{"disambiguationData":[TD([[makeQuery(id+"F3.imprint","IMPRINT",EDGE,{"derivedFrom":sQuery(id+"F3.wireOp",EDGE,"E8.13.0")}),1.0]])]});
            extrude(context, id + "F6", {"entities" : qUnion([Q0, Q1, Q2, Q3, Q4, Q5, Q6, Q7, Q8, Q9, Q10, Q11, Q12, Q13, Q14, Q15, Q16, Q17, Q18, Q19, Q20, Q21, Q22, Q23]), "operationType" : NewBodyOperationType.ADD, "depth" : getVariable(context, 'LED_lens_height'), "offsetDistance" : 25 * mm});
        }
    });
